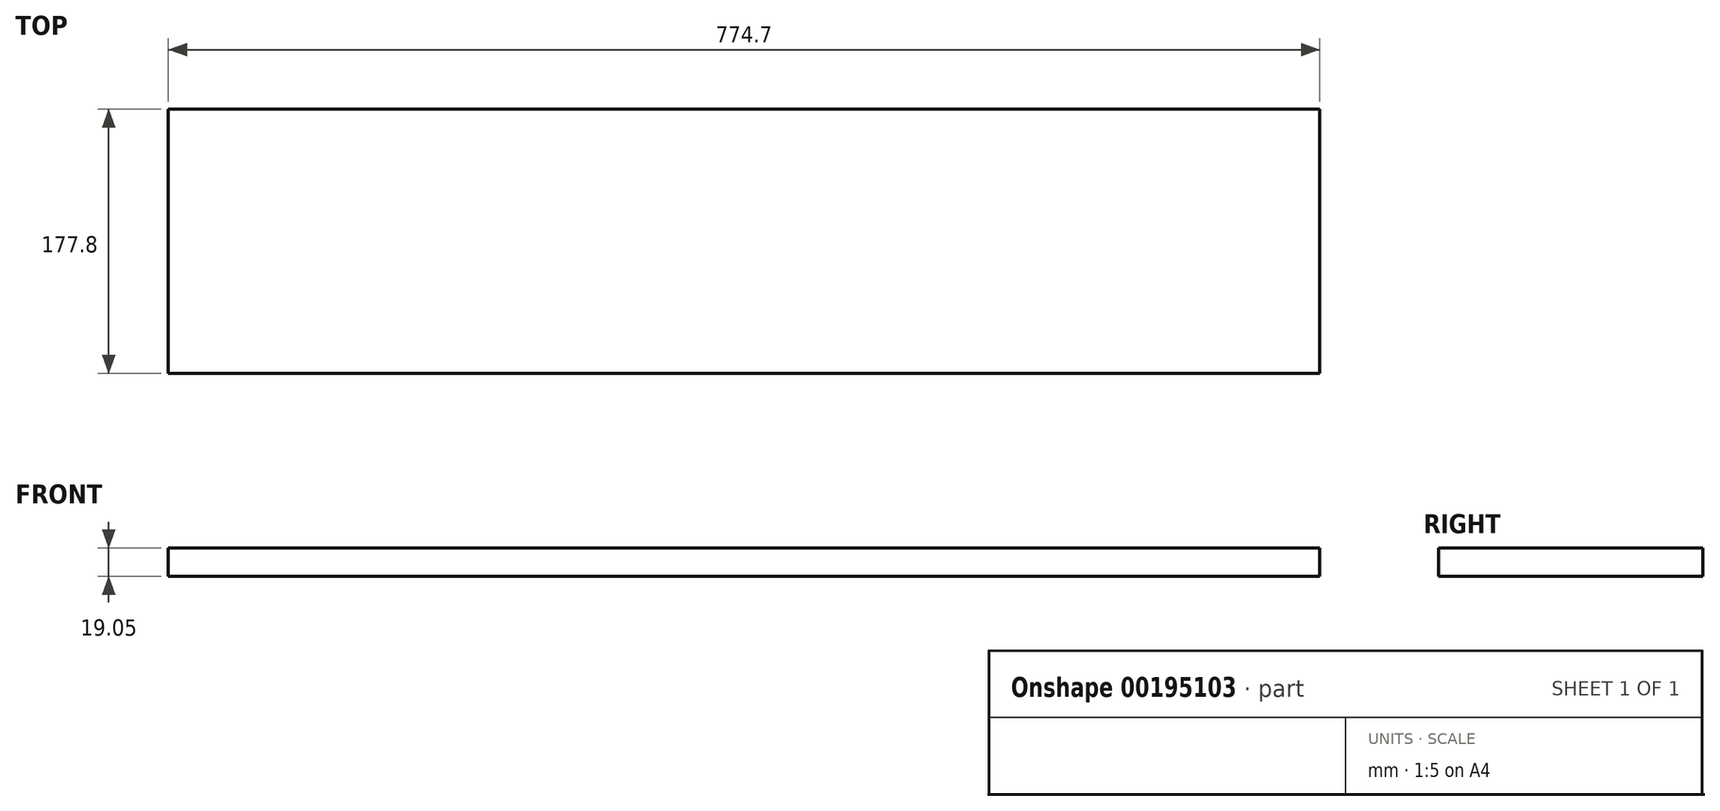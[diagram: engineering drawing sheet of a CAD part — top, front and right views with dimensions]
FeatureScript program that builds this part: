
annotation { "Feature Type Name" : "Feature", "Feature Type Description" : "" }
export const myFeature = defineFeature(function(context is Context, id is Id, definition is map)
    precondition{}
    {
        {
            var Q0;
            Q0=qCreatedBy(makeId("Top.planeOp"),FACE);
            var sketch = newSketch(context, id + "F0", { "sketchPlane" : qUnion([Q0])});
            skLineSegment(sketch, "E0.bottom", {"start": v(0, 0) * mm, "end": v(774.7, 0) * mm});
            skLineSegment(sketch, "E0.top", {"start": v(0, -177.8) * mm, "end": v(774.7, -177.8) * mm});
            skLineSegment(sketch, "E0.left", {"start": v(0, 0) * mm, "end": v(0, -177.8) * mm});
            skLineSegment(sketch, "E0.right", {"start": v(774.7, 0) * mm, "end": v(774.7, -177.8) * mm});
            skSolve(sketch);
        }
        {
            var Q0;
            Q0=makeQuery(id+"F0.imprint","IMPRINT",FACE,{"disambiguationData":[TD([[makeQuery(id+"F0.imprint","IMPRINT",EDGE,{"derivedFrom":sQuery(id+"F0.wireOp",EDGE,"E0.bottom")}),-1.0]])]});
            extrude(context, id + "F1", {"entities" : qUnion([Q0]), "depth" : 19.05 * mm});
        }
    });
